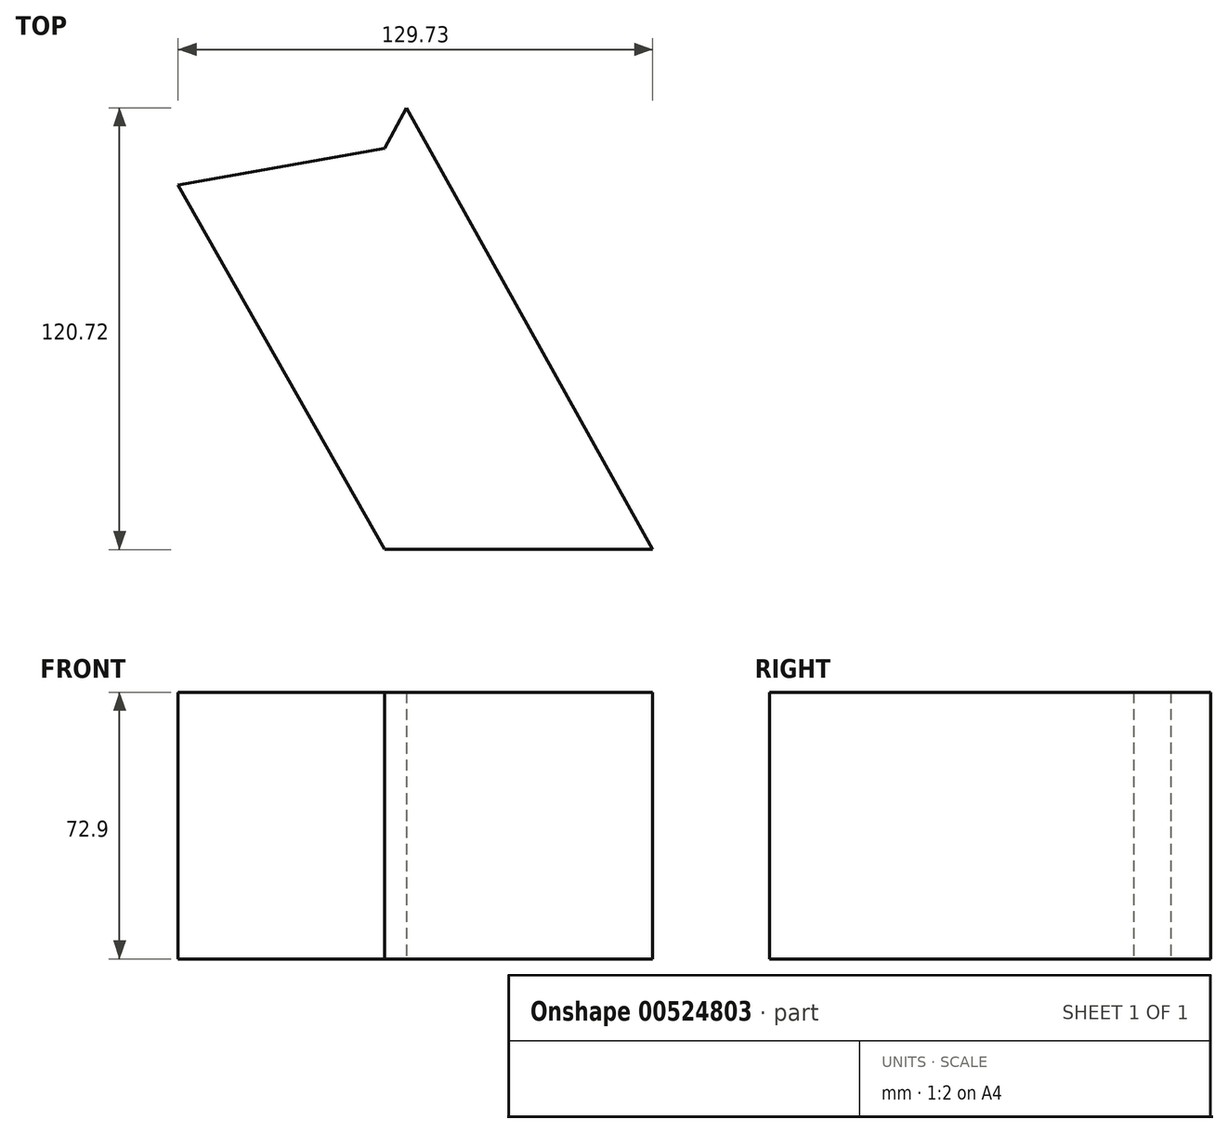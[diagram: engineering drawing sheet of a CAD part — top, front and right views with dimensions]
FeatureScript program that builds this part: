
annotation { "Feature Type Name" : "Feature", "Feature Type Description" : "" }
export const myFeature = defineFeature(function(context is Context, id is Id, definition is map)
    precondition{}
    {
        {
            var Q0;
            Q0=qCreatedBy(makeId("Top.planeOp"),FACE);
            var sketch = newSketch(context, id + "F0", { "sketchPlane" : qUnion([Q0])});
            skLineSegment(sketch, "E0", {"start": v(-97.9, 63.4) * mm, "end": v(-41.46, -36.2) * mm});
            skLineSegment(sketch, "E1", {"start": v(-41.46, -36.2) * mm, "end": v(31.83, -36.2) * mm});
            skLineSegment(sketch, "E2", {"start": v(-35.47, 84.52) * mm, "end": v(31.83, -36.2) * mm});
            skLineSegment(sketch, "E3", {"start": v(-41.46, 73.5) * mm, "end": v(-97.9, 63.4) * mm});
            skLineSegment(sketch, "E4", {"start": v(-41.46, 73.5) * mm, "end": v(-35.47, 84.52) * mm});
            skSolve(sketch);
        }
        {
            var Q0;
            Q0 = qSketchRegion(id + "F0", true);
            extrude(context, id + "F1", {"entities" : qUnion([Q0]), "depth" : 72.9 * mm, "offsetDistance" : 25.4 * mm});
        }
    });
